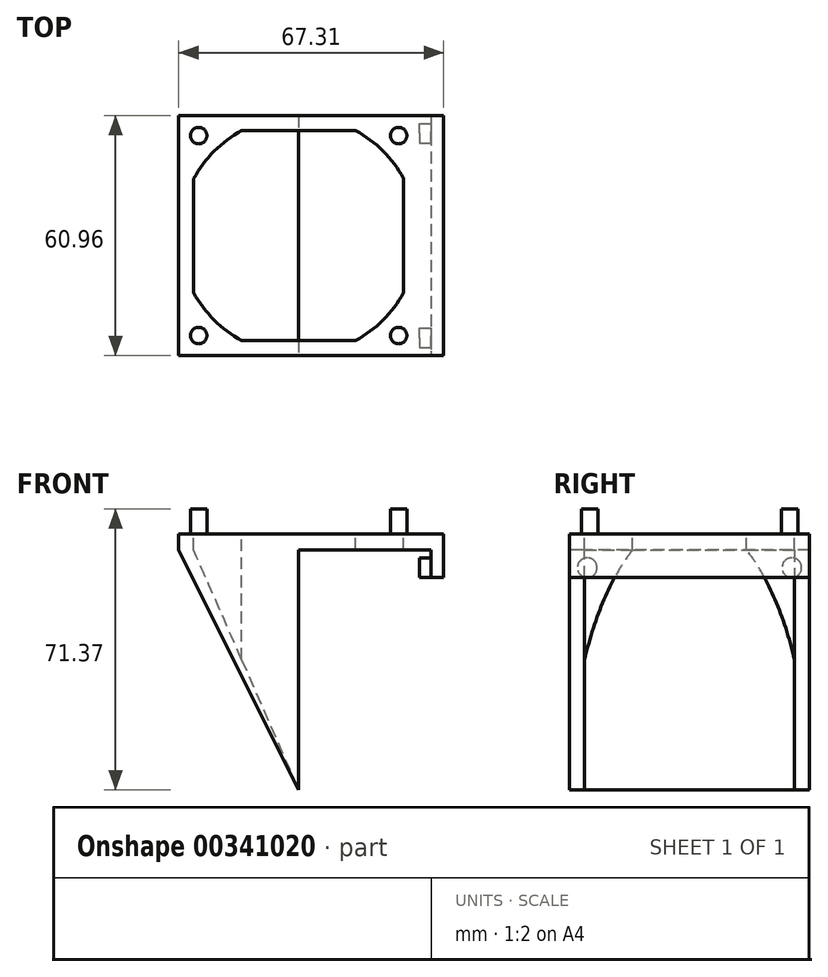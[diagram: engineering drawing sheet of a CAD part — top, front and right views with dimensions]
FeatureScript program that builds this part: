
annotation { "Feature Type Name" : "Feature", "Feature Type Description" : "" }
export const myFeature = defineFeature(function(context is Context, id is Id, definition is map)
    precondition{}
    {
        {
            var Q0;
            Q0=qCreatedBy(makeId("Right.planeOp"),FACE);
            var sketch = newSketch(context, id + "F0", { "sketchPlane" : qUnion([Q0])});
            skLineSegment(sketch, "E0.bottom", {"start": v(-27.89, 24.57) * mm, "end": v(33.07, 24.57) * mm});
            skLineSegment(sketch, "E0.top", {"start": v(-27.89, 20.5) * mm, "end": v(33.07, 20.5) * mm});
            skLineSegment(sketch, "E0.left", {"start": v(-27.89, 24.57) * mm, "end": v(-27.89, 20.5) * mm});
            skLineSegment(sketch, "E0.right", {"start": v(33.07, 24.57) * mm, "end": v(33.07, 20.5) * mm});
            skSolve(sketch);
        }
        {
            var Q0;
            Q0 = qSketchRegion(id + "F0", true);
            extrude(context, id + "F1", {"entities" : qUnion([Q0]), "depth" : 60.96 * mm});
        }
        {
            var Q0;
            Q0=makeQuery(id+"F1.opExtrude","SWEPT_FACE",FACE,{"disambiguationData":[OSD([sQuery(id+"F0.wireOp",EDGE,"E0.bottom")])]});
            var sketch = newSketch(context, id + "F2", { "sketchPlane" : qUnion([Q0])});
            skLineSegment(sketch, "E1.bottom", {"start": v(44.96, -24.08) * mm, "end": v(16, -24.08) * mm});
            skLineSegment(sketch, "E1.top", {"start": v(44.96, 29.26) * mm, "end": v(16, 29.26) * mm});
            skLineSegment(sketch, "E1.left", {"start": v(57.15, -11.89) * mm, "end": v(57.15, 17.07) * mm});
            skLineSegment(sketch, "E1.right", {"start": v(3.81, -11.89) * mm, "end": v(3.81, 17.07) * mm});
            skArc(sketch, "E2", {"start": v(3.8, -11.89) * mm, "mid": v(9.03, -18.86) * mm, "end": v(16, -24.08) * mm});
            skArc(sketch, "E3", {"start": v(16, 29.26) * mm, "mid": v(9.04, 24.03) * mm, "end": v(3.8, 17.07) * mm});
            skArc(sketch, "E4", {"start": v(57.15, 17.07) * mm, "mid": v(51.93, 24.04) * mm, "end": v(44.96, 29.26) * mm});
            skArc(sketch, "E5", {"start": v(44.96, -24.08) * mm, "mid": v(51.93, -18.86) * mm, "end": v(57.15, -11.89) * mm});
            skPoint(sketch, "E6.orphan", {"position": v(3.81, -24.08) * mm});
            skPoint(sketch, "E7.orphan", {"position": v(3.81, 29.26) * mm});
            skPoint(sketch, "E8.orphan", {"position": v(57.15, 29.26) * mm});
            skPoint(sketch, "E9.orphan", {"position": v(57.15, -24.08) * mm});
            skSolve(sketch);
        }
        {
            var Q0;
            Q0 = qSketchRegion(id + "F2", true);
            extrude(context, id + "F3", {"entities" : qUnion([Q0]), "operationType" : NewBodyOperationType.REMOVE, "oppositeDirection" : true, "depth" : 25.4 * mm});
        }
        {
            var Q0;
            Q0=makeQuery(id+"F1.opExtrude","SWEPT_FACE",FACE,{"disambiguationData":[OSD([sQuery(id+"F0.wireOp",EDGE,"E0.bottom")])]});
            var sketch = newSketch(context, id + "F4", { "sketchPlane" : qUnion([Q0])});
            skCircle(sketch, "E10", {"center": v(55.88, -22.8) * mm, "radius": 2.1 * mm});
            skCircle(sketch, "E11", {"center": v(55.88, 28) * mm, "radius": 2.1 * mm});
            skCircle(sketch, "E12", {"center": v(5.08, -22.8) * mm, "radius": 2.1 * mm});
            skCircle(sketch, "E13", {"center": v(5.08, 28) * mm, "radius": 2.1 * mm});
            skSolve(sketch);
        }
        {
            var Q0;
            Q0 = qSketchRegion(id + "F4", true);
            extrude(context, id + "F5", {"entities" : qUnion([Q0]), "operationType" : NewBodyOperationType.ADD, "depth" : 6.35 * mm});
        }
        {
            var Q0;
            Q0=makeQuery(id+"F1.opExtrude","SWEPT_FACE",FACE,{"disambiguationData":[OSD([sQuery(id+"F0.wireOp",EDGE,"E0.left")])]});
            var sketch = newSketch(context, id + "F6", { "sketchPlane" : qUnion([Q0])});
            skLineSegment(sketch, "E14", {"start": v(30.48, 20.5) * mm, "end": v(30.48, -40.45) * mm});
            skLineSegment(sketch, "E15", {"start": v(30.48, -40.45) * mm, "end": v(0, 20.5) * mm});
            skLineSegment(sketch, "E16", {"start": v(0, 20.5) * mm, "end": v(30.48, 20.5) * mm});
            skSolve(sketch);
        }
        {
            var Q0;
            Q0 = qSketchRegion(id + "F6", true);
            extrude(context, id + "F7", {"entities" : qUnion([Q0]), "operationType" : NewBodyOperationType.ADD, "oppositeDirection" : true, "depth" : 60.96 * mm});
        }
        {
            var Q0;
            {var subQ0=sQuery(id+"F6.wireOp",EDGE,"E14");var subQ1=sQuery(id+"F6.wireOp",EDGE,"E16");Q0=makeQuery(id+"F7.boolean.opBoolean","SPLIT",EDGE,{"disambiguationData":[topologyDisambiguationEdgeConnected([makeQuery(id+"F7.opExtrude","SWEPT_FACE",FACE,{"disambiguationData":[OSD([subQ0])]}),makeQuery(id+"F7.opExtrude","SWEPT_FACE",FACE,{"disambiguationData":[OSD([subQ1])]})])],"derivedFrom":makeQuery(id+"F7.opExtrude","SWEPT_EDGE",EDGE,{"disambiguationData":[OSD([sQuery(id+"F0.wireOp",EDGE,"E0.top"),sQuery(id+"F0.wireOp",EDGE,"E0.left"),subQ0,subQ1])]})});}
            chamfer(context, id + "F8", {"entities" : qUnion([Q0]), "chamferType" : ChamferType.TWO_OFFSETS, "width1" : 60.96 * mm, "oppositeDirection" : false, "width2" : 26.67 * mm, "tangentPropagation" : true});
        }
        {
            var Q0;
            Q0=makeQuery(id+"F1.opExtrude","CAP_FACE",FACE,{"disambiguationData":[OSD([sQuery(id+"F0.wireOp",EDGE,"E0.bottom"),sQuery(id+"F0.wireOp",EDGE,"E0.top"),sQuery(id+"F0.wireOp",EDGE,"E0.left"),sQuery(id+"F0.wireOp",EDGE,"E0.right")])],"isStart":false});
            var sketch = newSketch(context, id + "F9", { "sketchPlane" : qUnion([Q0])});
            skLineSegment(sketch, "E17.bottom", {"start": v(-27.89, 24.57) * mm, "end": v(33.07, 24.57) * mm});
            skLineSegment(sketch, "E17.top", {"start": v(-27.89, 20.5) * mm, "end": v(33.07, 20.5) * mm});
            skLineSegment(sketch, "E17.left", {"start": v(-27.89, 24.57) * mm, "end": v(-27.89, 20.5) * mm});
            skLineSegment(sketch, "E17.right", {"start": v(33.07, 24.57) * mm, "end": v(33.07, 20.5) * mm});
            skSolve(sketch);
        }
        {
            var Q0;
            Q0 = qSketchRegion(id + "F9", true);
            extrude(context, id + "F10", {"entities" : qUnion([Q0]), "operationType" : NewBodyOperationType.ADD, "depth" : 6.35 * mm});
        }
        {
            var Q0;
            Q0=makeQuery(id+"F10.boolean.opBoolean","MERGE",FACE,{"derivedFrom":[makeQuery(id+"F1.opExtrude","SWEPT_FACE",FACE,{"disambiguationData":[OSD([sQuery(id+"F0.wireOp",EDGE,"E0.top")])]}),makeQuery(id+"F10.opExtrude","SWEPT_FACE",FACE,{"disambiguationData":[OSD([sQuery(id+"F9.wireOp",EDGE,"E17.top")])]})]});
            var sketch = newSketch(context, id + "F11", { "sketchPlane" : qUnion([Q0])});
            skLineSegment(sketch, "E18.bottom", {"start": v(67.3, -33.07) * mm, "end": v(64.13, -33.07) * mm});
            skLineSegment(sketch, "E18.top", {"start": v(67.3, 27.89) * mm, "end": v(64.13, 27.89) * mm});
            skLineSegment(sketch, "E18.left", {"start": v(67.3, -33.07) * mm, "end": v(67.3, 27.89) * mm});
            skLineSegment(sketch, "E18.right", {"start": v(64.13, -33.07) * mm, "end": v(64.13, 27.89) * mm});
            skSolve(sketch);
        }
        {
            var Q0;
            Q0 = qSketchRegion(id + "F11", true);
            extrude(context, id + "F12", {"entities" : qUnion([Q0]), "operationType" : NewBodyOperationType.ADD, "depth" : 7 * mm});
        }
        {
            var Q0;
            Q0=makeQuery(id+"F12.opExtrude","SWEPT_FACE",FACE,{"disambiguationData":[OSD([sQuery(id+"F11.wireOp",EDGE,"E18.right")])]});
            var sketch = newSketch(context, id + "F13", { "sketchPlane" : qUnion([Q0])});
            skCircle(sketch, "E19", {"center": v(-28.57, 16) * mm, "radius": 2.5 * mm});
            skSolve(sketch);
        }
        {
            var Q0;
            Q0 = qSketchRegion(id + "F13", true);
            extrude(context, id + "F14", {"entities" : qUnion([Q0]), "operationType" : NewBodyOperationType.ADD, "depth" : 3 * mm});
        }
        {
            var Q0;
            Q0=makeQuery(id+"F12.opExtrude","SWEPT_FACE",FACE,{"disambiguationData":[OSD([sQuery(id+"F11.wireOp",EDGE,"E18.right")])]});
            var sketch = newSketch(context, id + "F15", { "sketchPlane" : qUnion([Q0])});
            skCircle(sketch, "E20", {"center": v(23.39, 16) * mm, "radius": 2.5 * mm});
            skSolve(sketch);
        }
        {
            var Q0;
            Q0 = qSketchRegion(id + "F15", true);
            extrude(context, id + "F16", {"entities" : qUnion([Q0]), "operationType" : NewBodyOperationType.ADD, "depth" : 3 * mm});
        }
    });
